# Revit family: Izveshchatel okhrannyy tochechnyy magnitokontaktnyy IO 102-43
name_source: partatom
category: Датчики
units: mm (PartAtom-declared; Revit-internal decimal feet)

## family parameters
Всегда вертикально = Да
Заголовок OmniClass = Communication and Data Processing Equipment
На основе рабочей плоскости = Нет
Номер OmniClass = 23.85.50.17
Общий = Нет
При загрузке вырезать с полостями = Нет
Размер круглого соединителя = Использовать диаметр
Сохранять ориентацию аннотаций = Нет
Тип детали = Нормальный
Точка принадлежности помещению = Нет

## types (1)
- ИО 102-43 «НЕРЖАВЕЙКА»
    ADSK_Единица измерения = шт.
    ADSK_Завод-изготовитель = ООО НПП «МАГНИТО-КОНТАКТ»
    ADSK_Масса = 0.02
    ADSK_Материал = Нержавеющая сталь
    ADSK_Наименование = Извещатель охранный точечный магнитоконтактный ИО 102-43 «НЕРЖАВЕЙКА»
    ADSK_Обозначение = ПАШК 425119.069
    ADSK_Размер_Высота = 8 мм
    ADSK_Размер_Длина = 75 мм
    ADSK_Размер_Ширина = 11 мм
    URL = https://m-kontakt.ru
    Диапазон рабочих температур, °С = от -50 до +50
    Изготовитель = ООО НПП «МАГНИТО-КОНТАКТ»
    Коммутируемое напряжение, В = от 0,02 до 72
    Коммутируемый ток, мА = от 1 до 250
    Описание = Извещатели предназначены для обнаружения несанкционированного открывания или перемещения охраняемых конструкций (дверей, окон, шкафов, сейфов, ячеек, выдвижных ящиков и т.п.), выполненных из магнитных материалов (стали и сплавов), с последующей выдачей извещения о тревоге на приемно-контрольный прибор или оконечное объектовое устройство системы передачи извещений по ГОСТ Р 52435-2015.
    Отметка по умолчанию = 0 мм
    Сопротивление замкнутых контактов, Ом, не более = 0.5
    Срок службы, лет = 8
    Степень защиты, обеспечиваемая оболочкой = IP68
